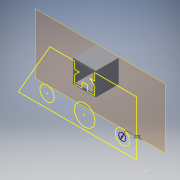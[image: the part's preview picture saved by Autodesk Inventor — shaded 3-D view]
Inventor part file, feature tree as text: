
AUTODESK INVENTOR PART (.ipt)
format: ipt  version: 2016 (Build 200138000, 138)  size: 111,616 bytes
history: native  units: in
note: dims shown in document units (in); Inventor stores cm internally (conversion verified against a paired STEP export)
features: reference x5, sketch x2, plane x1, extrude x1
ambient origin geometry x8: Origin, YZ Plane, XZ Plane, XY Plane, X Axis, Y Axis, Z Axis, Center Point
bodies: Solid1 (feature_tree)
feature tree (9):
  plane  "Work Plane1"
  extrude  "Extrusion1"  Depth=0.7874in
  sketch  "Sketch2"  dims[d2=1.0in d3=1.0in d4=1.0in d5=0.0in d6=0.315in]
  sketch  "Sketch1"  dims[d0=0.7874in d1=0.7874in]
  reference  "Reference1"
  reference  "Reference2"
  reference  "Reference3"
  reference  "Reference4"
  reference  "Reference5"
